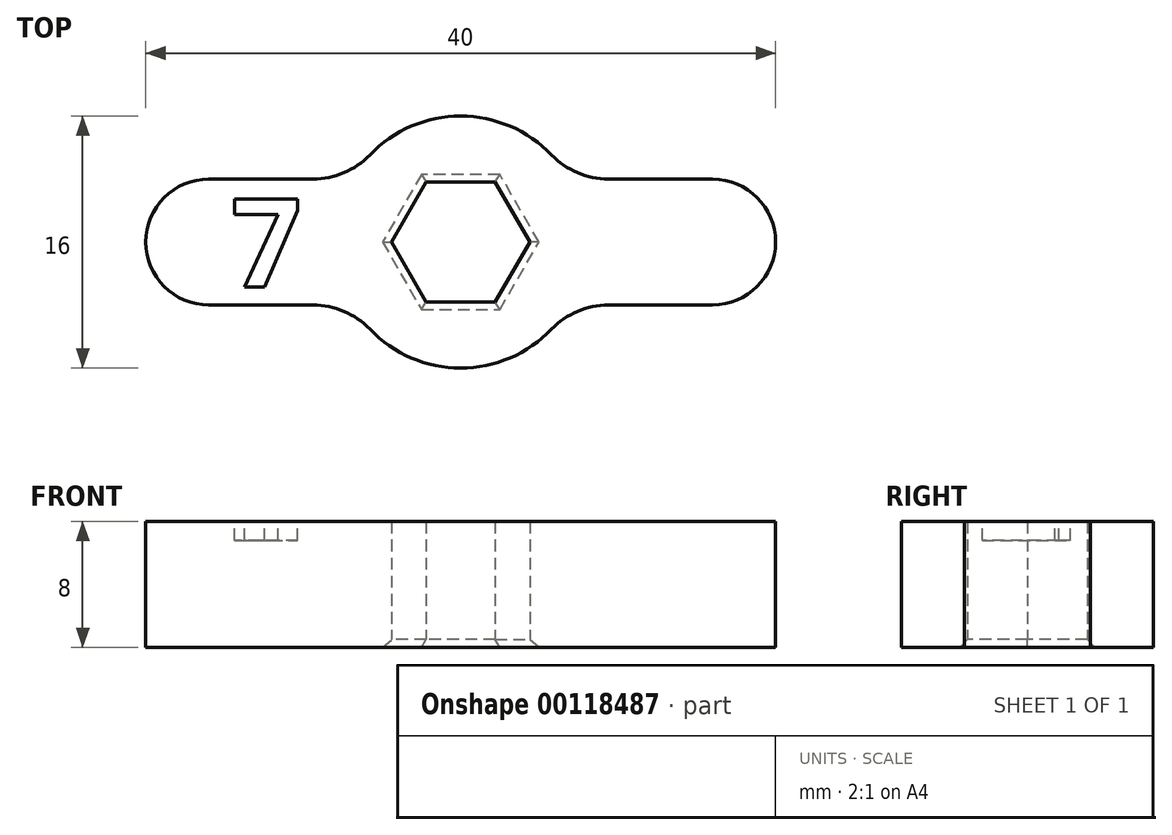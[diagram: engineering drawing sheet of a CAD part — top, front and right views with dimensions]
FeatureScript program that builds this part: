
annotation { "Feature Type Name" : "Feature", "Feature Type Description" : "" }
export const myFeature = defineFeature(function(context is Context, id is Id, definition is map)
    precondition{}
    {
        {
            var Q0;
            Q0=qCreatedBy(makeId("Top.planeOp"),FACE);
            var sketch = newSketch(context, id + "F0", { "sketchPlane" : qUnion([Q0])});
            skCircle(sketch, "E0.cCircle", {"center": v(-4.42, 4.13) * mm, "radius": 3.8 * mm, "construction": true});
            skLineSegment(sketch, "E0.0", {"start": v(-0.03, 4.13) * mm, "end": v(-2.22, 0.33) * mm});
            skLineSegment(sketch, "E0.1", {"start": v(-2.22, 0.33) * mm, "end": v(-6.61, 0.33) * mm});
            skLineSegment(sketch, "E0.2", {"start": v(-6.61, 0.33) * mm, "end": v(-8.8, 4.13) * mm});
            skLineSegment(sketch, "E0.3", {"start": v(-8.8, 4.13) * mm, "end": v(-6.61, 7.93) * mm});
            skLineSegment(sketch, "E0.4", {"start": v(-6.61, 7.93) * mm, "end": v(-2.22, 7.93) * mm});
            skLineSegment(sketch, "E0.5", {"start": v(-2.22, 7.93) * mm, "end": v(-0.03, 4.13) * mm});
            skPoint(sketch, "E0.0.midPoint", {"position": v(-1.13, 2.23) * mm});
            skCircle(sketch, "E1", {"center": v(-4.42, 4.13) * mm, "radius": 8 * mm});
            skLineSegment(sketch, "E2.bottom", {"start": v(2.51, 8.13) * mm, "end": v(11.58, 8.13) * mm});
            skLineSegment(sketch, "E2.top", {"start": v(2.51, 0.13) * mm, "end": v(11.58, 0.13) * mm});
            skArc(sketch, "E3", {"start": v(11.58, 8.13) * mm, "mid": v(15.58, 4.13) * mm, "end": v(11.58, 0.13) * mm});
            skLineSegment(sketch, "E4", {"start": v(-4.42, 13.39) * mm, "end": v(-4.42, -5.1) * mm, "construction": true});
            skLineSegment(sketch, "E5.MirrorCS", {"start": v(-11.35, 8.13) * mm, "end": v(-20.42, 8.13) * mm});
            skArc(sketch, "E6.MirrorCS", {"start": v(-20.42, 8.13) * mm, "mid": v(-24.42, 4.13) * mm, "end": v(-20.42, 0.13) * mm});
            skLineSegment(sketch, "E7.MirrorCS", {"start": v(-11.35, 0.13) * mm, "end": v(-20.42, 0.13) * mm});
            skLineSegment(sketch, "E8", {"start": v(-20.42, 4.13) * mm, "end": v(11.58, 4.13) * mm, "construction": true});
            skSolve(sketch);
        }
        {
            var Q0;
            {var subQ0=sQuery(id+"F0.wireOp",EDGE,"E5.MirrorCS");Q0=makeQuery(id+"F0.imprint","IMPRINT",FACE,{"disambiguationData":[TD([[makeQuery(id+"F0.imprint","IMPRINT",EDGE,{"derivedFrom":subQ0}),1.0]])]});}
            var Q1;
            Q1=makeQuery(id+"F0.imprint","IMPRINT",FACE,{"disambiguationData":[TD([[makeQuery(id+"F0.imprint","IMPRINT",EDGE,{"derivedFrom":sQuery(id+"F0.wireOp",EDGE,"E0.0")}),1.0]])]});
            var Q2;
            {var subQ0=sQuery(id+"F0.wireOp",EDGE,"E2.bottom");Q2=makeQuery(id+"F0.imprint","IMPRINT",FACE,{"disambiguationData":[TD([[makeQuery(id+"F0.imprint","IMPRINT",EDGE,{"derivedFrom":subQ0}),-1.0]])]});}
            extrude(context, id + "F1", {"entities" : qUnion([Q0, Q1, Q2]), "depth" : 8 * mm});
        }
        {
            var Q0;
            Q0=makeQuery(id+"F1.opExtrude","CAP_FACE",FACE,{"disambiguationData":[OSD([sQuery(id+"F0.wireOp",EDGE,"E0.0"),sQuery(id+"F0.wireOp",EDGE,"E0.1"),sQuery(id+"F0.wireOp",EDGE,"E0.2"),sQuery(id+"F0.wireOp",EDGE,"E0.3"),sQuery(id+"F0.wireOp",EDGE,"E0.4"),sQuery(id+"F0.wireOp",EDGE,"E0.5"),sQuery(id+"F0.wireOp",EDGE,"E1"),sQuery(id+"F0.wireOp",EDGE,"E2.bottom"),sQuery(id+"F0.wireOp",EDGE,"E2.top"),sQuery(id+"F0.wireOp",EDGE,"E3"),sQuery(id+"F0.wireOp",EDGE,"E5.MirrorCS"),sQuery(id+"F0.wireOp",EDGE,"E6.MirrorCS"),sQuery(id+"F0.wireOp",EDGE,"E7.MirrorCS")])],"isStart":false});
            var sketch = newSketch(context, id + "F2", { "sketchPlane" : qUnion([Q0])});
            skText(sketch, "E9", { "text": "7", "fontName": "OpenSans-Bold.ttf"});
            skLineSegment(sketch, "E10.0", {"start": v(-20.42, 4.13) * mm, "end": v(11.58, 4.13) * mm, "construction": true});
            const initialGuessF2  = {"E9": [-0.019, 0.00126, 1, 0, 0.00566]};
            skSetInitialGuess(sketch, initialGuessF2);
            skSolve(sketch);
        }
        {
            var Q0;
            Q0 = qSketchRegion(id + "F2", true);
            extrude(context, id + "F3", {"entities" : qUnion([Q0]), "operationType" : NewBodyOperationType.REMOVE, "oppositeDirection" : true, "depth" : 1.2 * mm});
        }
        {
            var Q0;
            Q0=makeQuery(id+"F1.opExtrude","SWEPT_EDGE",EDGE,{"disambiguationData":[OSD([sQuery(id+"F0.wireOp",EDGE,"E1"),sQuery(id+"F0.wireOp",EDGE,"E2.top")])]});
            var Q1;
            Q1=makeQuery(id+"F1.opExtrude","SWEPT_EDGE",EDGE,{"disambiguationData":[OSD([sQuery(id+"F0.wireOp",EDGE,"E1"),sQuery(id+"F0.wireOp",EDGE,"E7.MirrorCS")])]});
            var Q2;
            Q2=makeQuery(id+"F1.opExtrude","SWEPT_EDGE",EDGE,{"disambiguationData":[OSD([sQuery(id+"F0.wireOp",EDGE,"E1"),sQuery(id+"F0.wireOp",EDGE,"E2.bottom")])]});
            var Q3;
            Q3=makeQuery(id+"F1.opExtrude","SWEPT_EDGE",EDGE,{"disambiguationData":[OSD([sQuery(id+"F0.wireOp",EDGE,"E1"),sQuery(id+"F0.wireOp",EDGE,"E5.MirrorCS")])]});
            fillet(context, id + "F4", {"entities" : qUnion([Q0, Q1, Q2, Q3]), "radius" : 5 * mm, "tangentPropagation" : true, "allowEdgeOverflow" : false});
        }
        {
            var Q0;
            Q0=makeQuery(id+"F1.opExtrude","CAP_EDGE",EDGE,{"disambiguationData":[OSD([sQuery(id+"F0.wireOp",EDGE,"E0.1")])],"isStart":true});
            var Q1;
            Q1=makeQuery(id+"F1.opExtrude","CAP_EDGE",EDGE,{"disambiguationData":[OSD([sQuery(id+"F0.wireOp",EDGE,"E0.2")])],"isStart":true});
            var Q2;
            Q2=makeQuery(id+"F1.opExtrude","CAP_EDGE",EDGE,{"disambiguationData":[OSD([sQuery(id+"F0.wireOp",EDGE,"E0.3")])],"isStart":true});
            var Q3;
            Q3=makeQuery(id+"F1.opExtrude","CAP_EDGE",EDGE,{"disambiguationData":[OSD([sQuery(id+"F0.wireOp",EDGE,"E0.4")])],"isStart":true});
            var Q4;
            Q4=makeQuery(id+"F1.opExtrude","CAP_EDGE",EDGE,{"disambiguationData":[OSD([sQuery(id+"F0.wireOp",EDGE,"E0.5")])],"isStart":true});
            var Q5;
            Q5=makeQuery(id+"F1.opExtrude","CAP_EDGE",EDGE,{"disambiguationData":[OSD([sQuery(id+"F0.wireOp",EDGE,"E0.0")])],"isStart":true});
            chamfer(context, id + "F5", {"entities" : qUnion([Q0, Q1, Q2, Q3, Q4, Q5]), "width" : 0.5 * mm, "tangentPropagation" : true});
        }
    });
